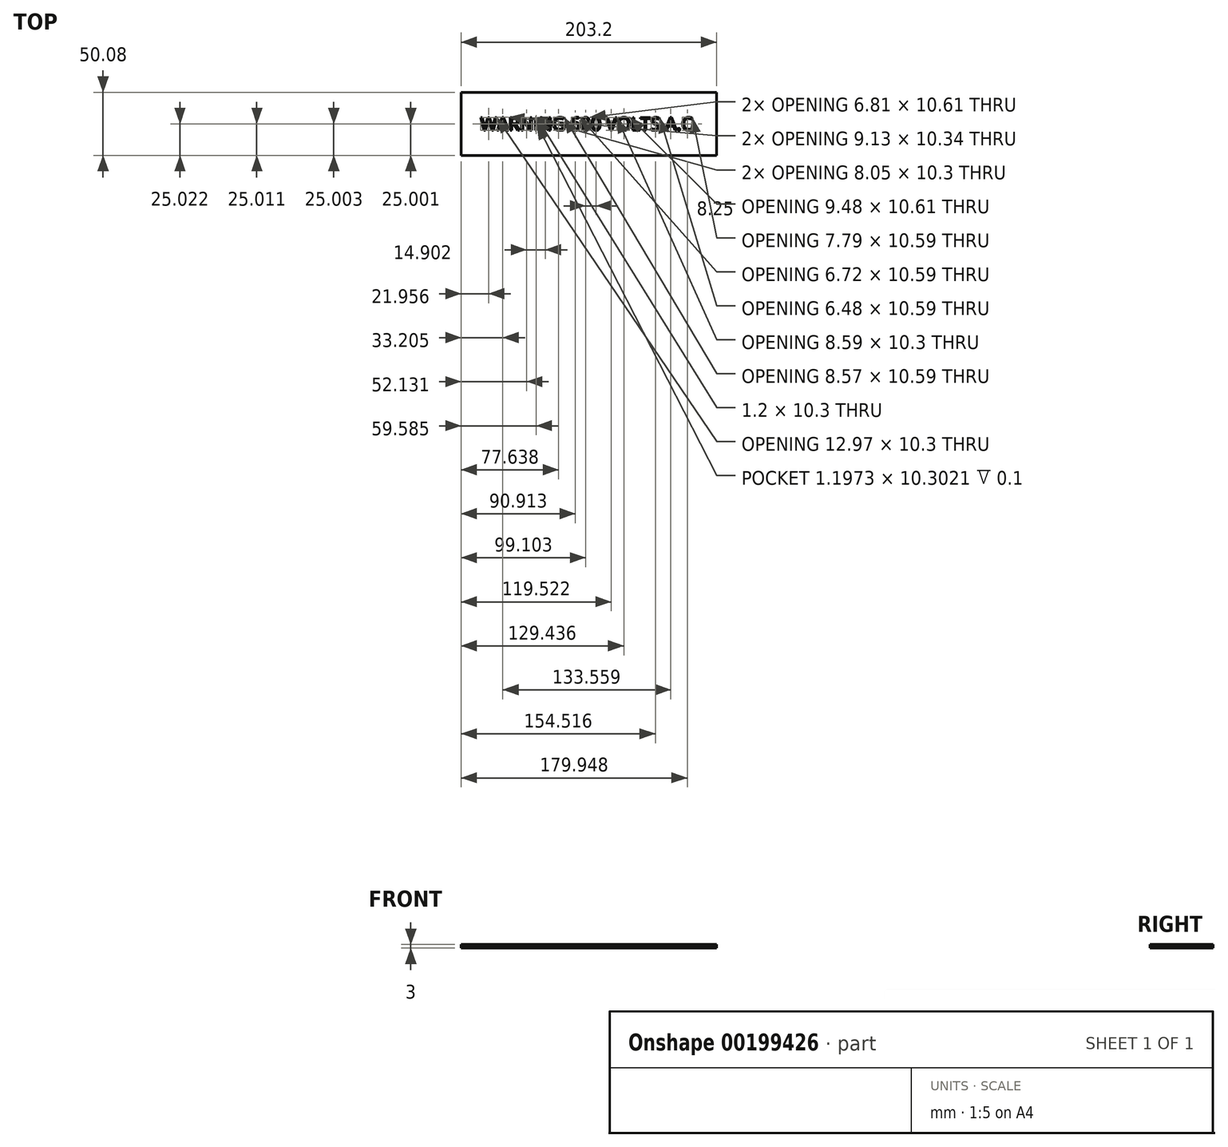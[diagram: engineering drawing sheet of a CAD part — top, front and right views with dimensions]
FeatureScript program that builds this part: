
annotation { "Feature Type Name" : "Feature", "Feature Type Description" : "" }
export const myFeature = defineFeature(function(context is Context, id is Id, definition is map)
    precondition{}
    {
        {
            var Q0;
            Q0=qCreatedBy(makeId("Top.planeOp"),FACE);
            var sketch = newSketch(context, id + "F0", { "sketchPlane" : qUnion([Q0])});
            skLineSegment(sketch, "E0.bottom", {"start": v(-25.7, -9.9) * mm, "end": v(177.5, -9.9) * mm});
            skLineSegment(sketch, "E0.top", {"start": v(-25.7, 40.17) * mm, "end": v(177.5, 40.17) * mm});
            skLineSegment(sketch, "E0.left", {"start": v(-25.7, -9.9) * mm, "end": v(-25.7, 40.17) * mm});
            skLineSegment(sketch, "E0.right", {"start": v(177.5, -9.9) * mm, "end": v(177.5, 40.17) * mm});
            skSolve(sketch);
        }
        {
            var Q0;
            Q0=makeQuery(id+"F0.imprint","IMPRINT",FACE,{"disambiguationData":[TD([[makeQuery(id+"F0.imprint","IMPRINT",EDGE,{"derivedFrom":sQuery(id+"F0.wireOp",EDGE,"E0.bottom")}),1.0]])]});
            extrude(context, id + "F1", {"entities" : qUnion([Q0]), "depth" : 2 * mm});
        }
        {
            var Q0;
            Q0=makeQuery(id+"F1.opExtrude","CAP_FACE",FACE,{"disambiguationData":[OSD([sQuery(id+"F0.wireOp",EDGE,"E0.bottom"),sQuery(id+"F0.wireOp",EDGE,"E0.top"),sQuery(id+"F0.wireOp",EDGE,"E0.left"),sQuery(id+"F0.wireOp",EDGE,"E0.right")])],"isStart":false});
            extrude(context, id + "F2", {"entities" : qUnion([Q0]), "depth" : 1 * mm});
        }
        {
            var Q0;
            Q0=makeQuery(id+"F2.opExtrude","CAP_FACE",FACE,{"disambiguationData":[OSD([sQuery(id+"F0.wireOp",EDGE,"E0.bottom"),sQuery(id+"F0.wireOp",EDGE,"E0.top"),sQuery(id+"F0.wireOp",EDGE,"E0.left"),sQuery(id+"F0.wireOp",EDGE,"E0.right")])],"isStart":false});
            var sketch = newSketch(context, id + "F3", { "sketchPlane" : qUnion([Q0])});
            skText(sketch, "E1", { "text": "WARNING 600 VOLTS A.C.", "fontName": "OpenSans-Regular.ttf"});
            const initialGuessF3  = {"E1": [-0.01043, 0.00994, 1, 0, 0.01039]};
            skSetInitialGuess(sketch, initialGuessF3);
            skSolve(sketch);
        }
        {
            var Q0;
            Q0 = qSketchRegion(id + "F3", true);
            extrude(context, id + "F4", {"entities" : qUnion([Q0]), "operationType" : NewBodyOperationType.REMOVE, "oppositeDirection" : true, "depth" : 1.1 * mm});
        }
    });
